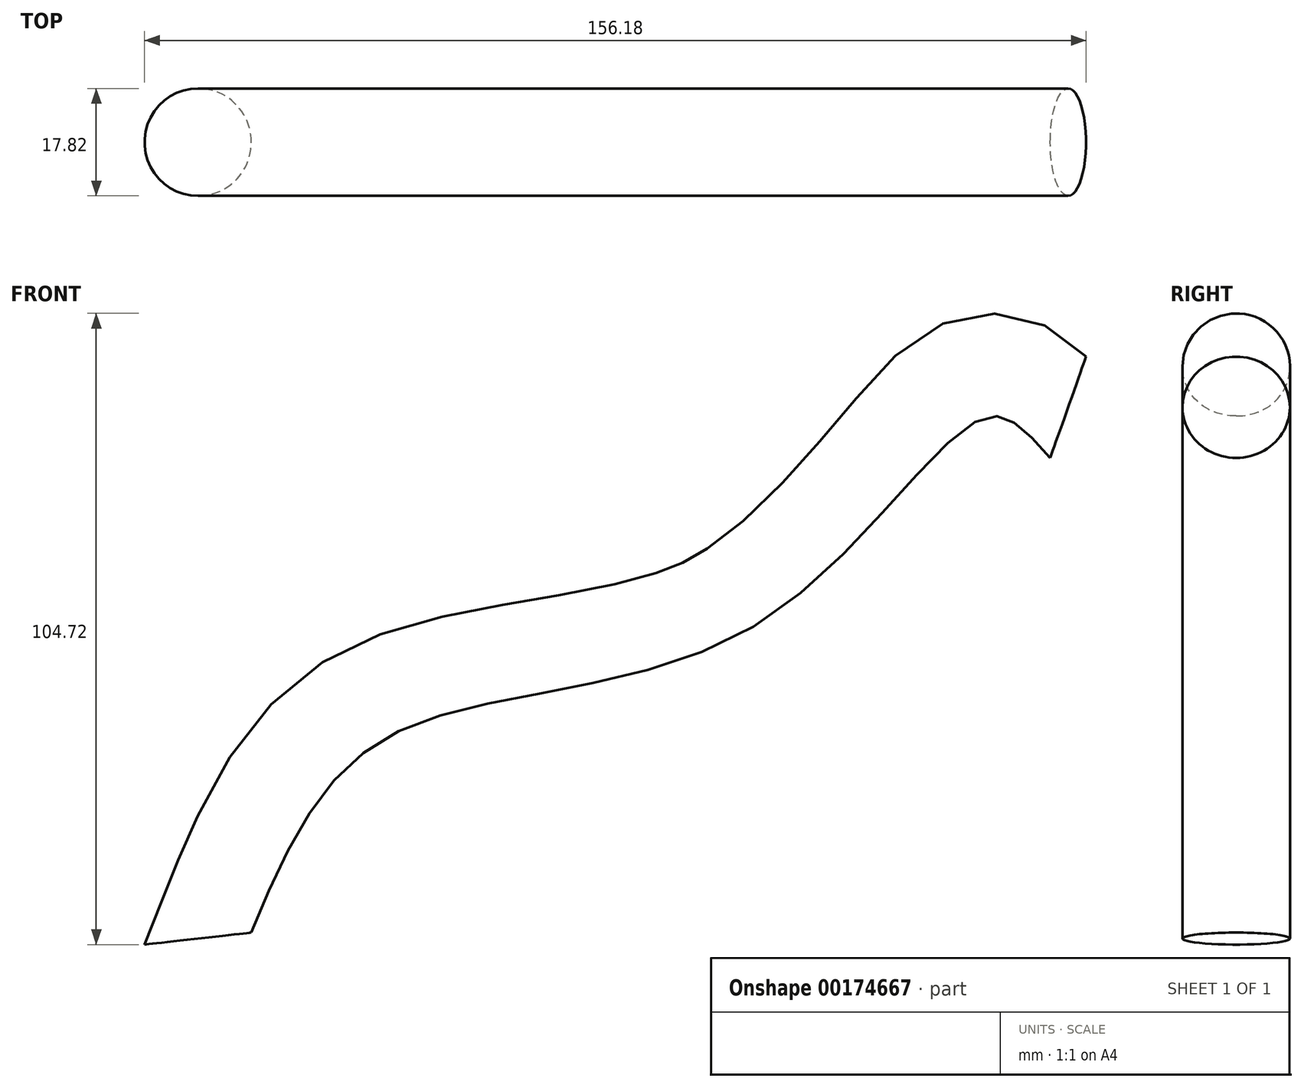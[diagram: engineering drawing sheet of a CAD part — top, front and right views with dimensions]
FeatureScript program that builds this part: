
annotation { "Feature Type Name" : "Feature", "Feature Type Description" : "" }
export const myFeature = defineFeature(function(context is Context, id is Id, definition is map)
    precondition{}
    {
        {
            var Q0;
            Q0=qCreatedBy(makeId("Front.planeOp"),FACE);
            var sketch = newSketch(context, id + "F0", { "sketchPlane" : qUnion([Q0])});
            skFitSpline(sketch, "E0", {"points": [v(-65.02, -16.5) * mm, v(-41.52, 17.22) * mm, v(19.27, 35.6) * mm, v(58.1, 70.35) * mm, v(69.34, 63.7) * mm], "startDerivative": vector(65.65, 158.82) * mm, "endDerivative": vector(71.94, -80.84) * mm});
            skSolve(sketch);
        }
        {
            var Q0;
            Q0=qCreatedBy(makeId("Top.planeOp"),FACE);
            var sketch = newSketch(context, id + "F1", { "sketchPlane" : qUnion([Q0])});
            skCircle(sketch, "E1", {"center": v(-65.02, 0) * mm, "radius": 8.91 * mm});
            skSolve(sketch);
        }
        {
            var Q0;
            Q0=makeQuery(id+"F1.imprint","IMPRINT",FACE,{"disambiguationData":[TD([[makeQuery(id+"F1.imprint","IMPRINT",EDGE,{"derivedFrom":sQuery(id+"F1.wireOp",EDGE,"E1")}),1.0]])]});
            var Q1;
            Q1=sQuery(id+"F0.wireOp",EDGE,"E0");
            sweep(context, id + "F2", {"profiles" : qUnion([Q0]), "path" : qUnion([Q1])});
        }
    });
